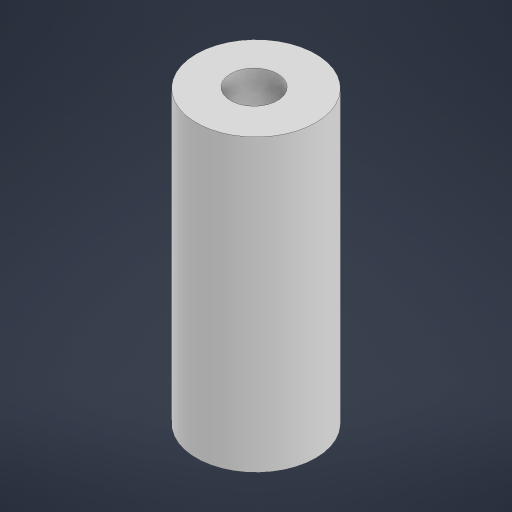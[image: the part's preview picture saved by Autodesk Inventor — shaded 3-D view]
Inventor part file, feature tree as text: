
AUTODESK INVENTOR PART (.ipt)
format: ipt  version: 2024.3 (Build 283343000, 343)  size: 157,696 bytes
history: native  units: in
note: dims shown in document units (in); Inventor stores cm internally (conversion verified against a paired STEP export)
features: extrude x1, sketch x1
ambient origin geometry x8: Origin, YZ Plane, XZ Plane, XY Plane, X Axis, Y Axis, Z Axis, Center Point
bodies: Solid1 (feature_tree)
feature tree (2):
  extrude  "Extrusion1"  Depth=1.217in
  sketch  "Sketch1"  dims[d0=0.5in d1=0.196in d2=1.217in d3=0.0in]
